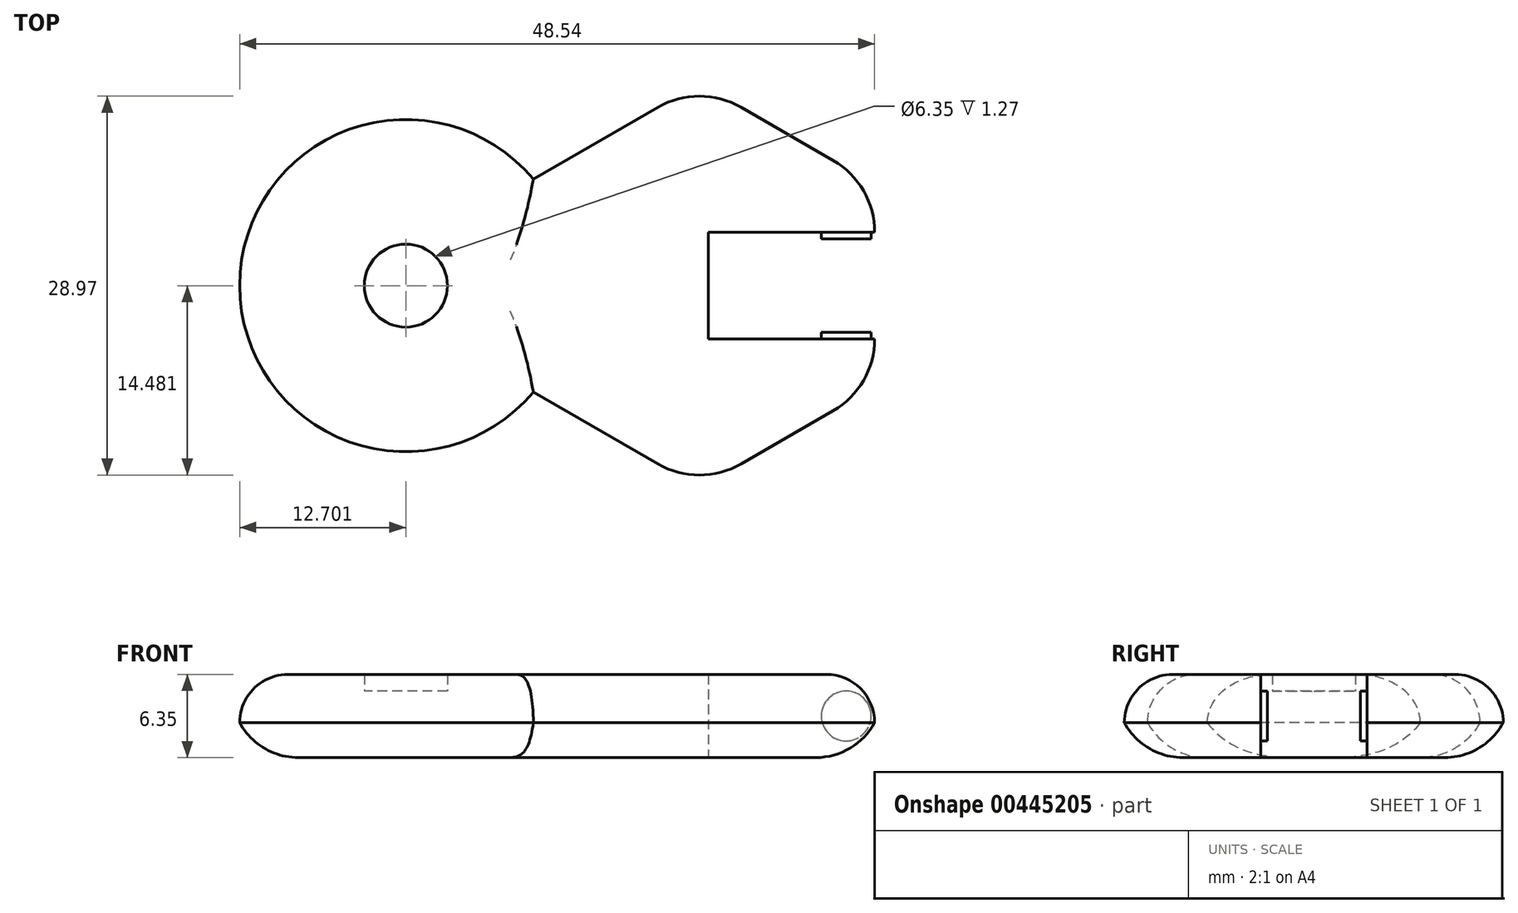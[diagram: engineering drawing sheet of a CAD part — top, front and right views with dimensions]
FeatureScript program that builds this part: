
annotation { "Feature Type Name" : "Feature", "Feature Type Description" : "" }
export const myFeature = defineFeature(function(context is Context, id is Id, definition is map)
    precondition{}
    {
        {
            var Q0;
            Q0=qCreatedBy(makeId("Top.planeOp"),FACE);
            var sketch = newSketch(context, id + "F0", { "sketchPlane" : qUnion([Q0])});
            skArc(sketch, "E0", {"start": v(-23.92, 38.55) * mm, "mid": v(-46.34, 29.5) * mm, "end": v(-22.85, 23.76) * mm});
            skArc(sketch, "E1.cCircle", {"start": v(-22.85, 23.76) * mm, "mid": v(-9.81, 17.1) * mm, "end": v(1.54, 26.34) * mm, "construction": true});
            skLineSegment(sketch, "E1.1", {"start": v(-24.62, 38.14) * mm, "end": v(-14.4, 44.05) * mm});
            skLineSegment(sketch, "E1.2", {"start": v(-8.05, 44.05) * mm, "end": v(-1, 39.98) * mm});
            skLineSegment(sketch, "E1.4", {"start": v(-1, 20.84) * mm, "end": v(-8.05, 16.78) * mm});
            skLineSegment(sketch, "E1.5", {"start": v(-14.4, 16.78) * mm, "end": v(-24.62, 22.68) * mm});
            skPoint(sketch, "E1.0.midPoint", {"position": v(-24.62, 30.41) * mm});
            skPoint(sketch, "E2.visualSharp", {"position": v(-11.22, 45.88) * mm});
            skArc(sketch, "E2.filletArc", {"start": v(-8.05, 44.05) * mm, "mid": v(-11.22, 44.9) * mm, "end": v(-14.4, 44.05) * mm});
            skPoint(sketch, "E3.visualSharp", {"position": v(2.17, 38.14) * mm});
            skArc(sketch, "E3.filletArc", {"start": v(2.17, 34.48) * mm, "mid": v(1.32, 37.65) * mm, "end": v(-1, 39.98) * mm});
            skPoint(sketch, "E4.visualSharp", {"position": v(2.17, 22.68) * mm});
            skArc(sketch, "E4.filletArc", {"start": v(-1, 20.84) * mm, "mid": v(1.32, 23.17) * mm, "end": v(2.17, 26.34) * mm});
            skPoint(sketch, "E5.visualSharp", {"position": v(-11.22, 14.94) * mm});
            skArc(sketch, "E5.filletArc", {"start": v(-14.4, 16.78) * mm, "mid": v(-11.22, 15.93) * mm, "end": v(-8.05, 16.78) * mm});
            skLineSegment(sketch, "E6.bottom", {"start": v(2.17, 34.48) * mm, "end": v(-10.53, 34.48) * mm});
            skLineSegment(sketch, "E6.top", {"start": v(2.17, 26.34) * mm, "end": v(-10.53, 26.34) * mm});
            skLineSegment(sketch, "E6.right", {"start": v(-10.53, 34.48) * mm, "end": v(-10.53, 26.34) * mm});
            skArc(sketch, "E7.trimOffspring", {"start": v(1.54, 34.48) * mm, "mid": v(-9.81, 43.73) * mm, "end": v(-22.85, 37.06) * mm, "construction": true});
            skCircle(sketch, "E8", {"center": v(-33.67, 30.41) * mm, "radius": 3.18 * mm});
            skSolve(sketch);
        }
        {
            var Q0;
            Q0=qSketchRegion(id+"F0",true);
            extrude(context, id + "F1", {"entities" : qUnion([Q0]), "depth" : 6.35 * mm});
        }
        {
            var Q0;
            Q0=makeQuery(id+"F1.opExtrude","SWEPT_FACE",FACE,{"disambiguationData":[OSD([sQuery(id+"F0.wireOp",EDGE,"E6.top")])]});
            var sketch = newSketch(context, id + "F2", { "sketchPlane" : qUnion([Q0])});
            skCircle(sketch, "E9", {"center": v(0, 3.18) * mm, "radius": 1.9 * mm});
            skPoint(sketch, "E9.centerSnap0", {"position": v(-2.17, 3.18) * mm});
            skSolve(sketch);
        }
        {
            var Q0;
            Q0=qSketchRegion(id+"F2",true);
            extrude(context, id + "F3", {"entities" : qUnion([Q0]), "operationType" : NewBodyOperationType.ADD, "depth" : 0.5 * mm});
        }
        {
            var Q0;
            Q0=makeQuery(id+"F1.opExtrude","SWEPT_FACE",FACE,{"disambiguationData":[OSD([sQuery(id+"F0.wireOp",EDGE,"E6.bottom")])]});
            var sketch = newSketch(context, id + "F4", { "sketchPlane" : qUnion([Q0])});
            skCircle(sketch, "E10", {"center": v(0, 3.18) * mm, "radius": 1.9 * mm});
            skPoint(sketch, "E10.centerSnap0", {"position": v(2.17, 3.18) * mm});
            skSolve(sketch);
        }
        {
            var Q0;
            Q0=qSketchRegion(id+"F4",true);
            extrude(context, id + "F5", {"entities" : qUnion([Q0]), "operationType" : NewBodyOperationType.ADD, "depth" : 0.5 * mm});
        }
        {
            var Q0;
            Q0=makeQuery(id+"F0.imprint","IMPRINT",FACE,{"disambiguationData":[TD([[makeQuery(id+"F0.imprint","IMPRINT",EDGE,{"derivedFrom":sQuery(id+"F0.wireOp",EDGE,"E8")}),1.0]])]});
            extrude(context, id + "F6", {"entities" : qUnion([Q0]), "operationType" : NewBodyOperationType.ADD, "depth" : 5.08 * mm});
        }
        {
            var Q0;
            Q0=makeQuery(id+"F1.opExtrude","CAP_EDGE",EDGE,{"disambiguationData":[OSD([sQuery(id+"F0.wireOp",EDGE,"E1.2")])],"isStart":false});
            var Q1;
            Q1=makeQuery(id+"F1.opExtrude","CAP_EDGE",EDGE,{"disambiguationData":[OSD([sQuery(id+"F0.wireOp",EDGE,"E3.filletArc")])],"isStart":false});
            var Q2;
            Q2=makeQuery(id+"F1.opExtrude","CAP_EDGE",EDGE,{"disambiguationData":[OSD([sQuery(id+"F0.wireOp",EDGE,"E0")])],"isStart":false});
            var Q3;
            Q3=makeQuery(id+"F1.opExtrude","CAP_EDGE",EDGE,{"disambiguationData":[OSD([sQuery(id+"F0.wireOp",EDGE,"E1.5")])],"isStart":false});
            fillet(context, id + "F7", {"entities" : qUnion([Q0, Q1, Q2, Q3]), "radius" : 3.68 * mm, "tangentPropagation" : true, "allowEdgeOverflow" : false});
        }
        {
            var Q0;
            Q0=makeQuery(id+"F1.opExtrude","CAP_EDGE",EDGE,{"disambiguationData":[OSD([sQuery(id+"F0.wireOp",EDGE,"E1.1")])],"isStart":true});
            var Q1;
            Q1=makeQuery(id+"F1.opExtrude","CAP_EDGE",EDGE,{"disambiguationData":[OSD([sQuery(id+"F0.wireOp",EDGE,"E2.filletArc")])],"isStart":true});
            var Q2;
            Q2=makeQuery(id+"F1.opExtrude","CAP_EDGE",EDGE,{"disambiguationData":[OSD([sQuery(id+"F0.wireOp",EDGE,"E0")])],"isStart":true});
            var Q3;
            Q3=makeQuery(id+"F1.opExtrude","CAP_EDGE",EDGE,{"disambiguationData":[OSD([sQuery(id+"F0.wireOp",EDGE,"E1.4")])],"isStart":true});
            fillet(context, id + "F8", {"entities" : qUnion([Q0, Q1, Q2, Q3]), "radius" : 5.08 * mm, "tangentPropagation" : true, "allowEdgeOverflow" : false});
        }
    });
